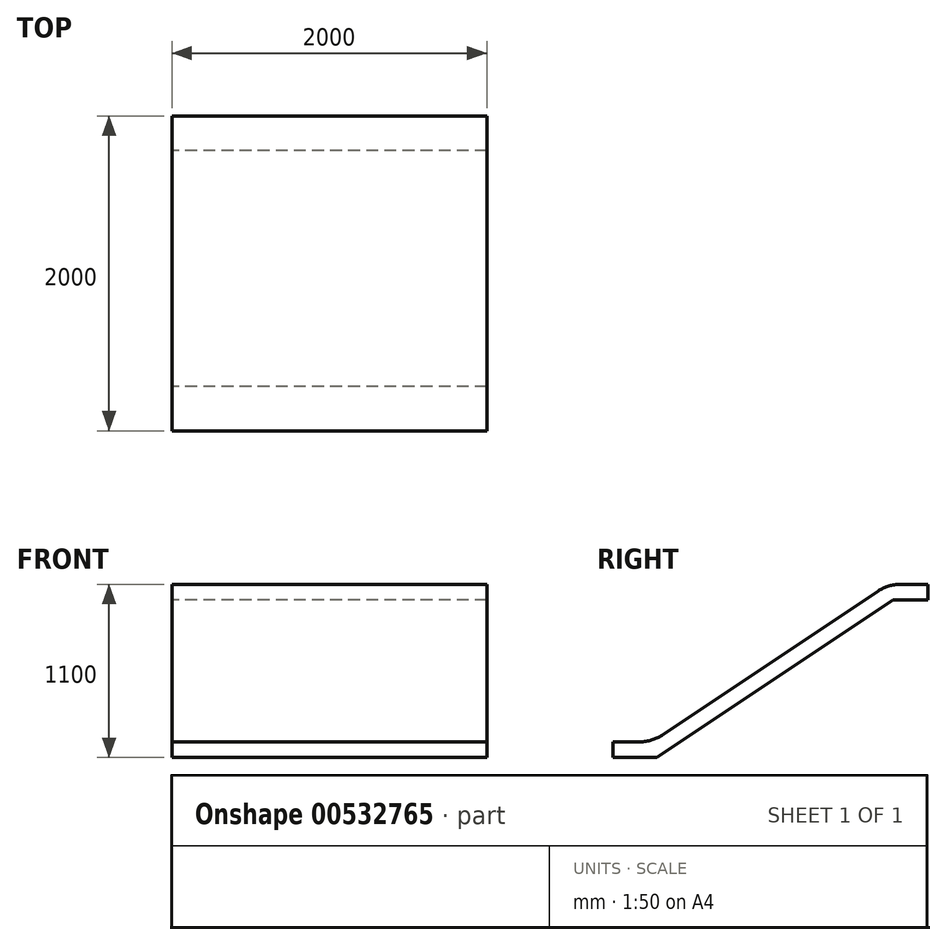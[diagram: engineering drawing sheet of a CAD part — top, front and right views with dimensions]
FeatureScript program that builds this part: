
annotation { "Feature Type Name" : "Feature", "Feature Type Description" : "" }
export const myFeature = defineFeature(function(context is Context, id is Id, definition is map)
    precondition{}
    {
        {
            var Q0;
            Q0=qCreatedBy(makeId("Right.planeOp"),FACE);
            var sketch = newSketch(context, id + "F0", { "sketchPlane" : qUnion([Q0])});
            skLineSegment(sketch, "E0", {"start": v(0, 0) * mm, "end": v(-250, 0) * mm});
            skLineSegment(sketch, "E1", {"start": v(-250, 0) * mm, "end": v(-1750, -1000) * mm});
            skLineSegment(sketch, "E2", {"start": v(-1750, -1000) * mm, "end": v(-2000, -1000) * mm});
            skLineSegment(sketch, "E3.0", {"start": v(-1719.72, -1100) * mm, "end": v(-2000, -1100) * mm});
            skLineSegment(sketch, "E3.1", {"start": v(-219.72, -100) * mm, "end": v(-1719.72, -1100) * mm});
            skLineSegment(sketch, "E3.2", {"start": v(0, -100) * mm, "end": v(-219.72, -100) * mm});
            skLineSegment(sketch, "E4", {"start": v(-2000, -1000) * mm, "end": v(-2000, -1100) * mm});
            skLineSegment(sketch, "E5", {"start": v(0, -100) * mm, "end": v(0, 0) * mm});
            skSolve(sketch);
        }
        {
            var Q0;
            Q0=makeQuery(id+"F0.imprint","IMPRINT",FACE,{"disambiguationData":[TD([[makeQuery(id+"F0.imprint","IMPRINT",EDGE,{"derivedFrom":sQuery(id+"F0.wireOp",EDGE,"E0")}),1.0]])]});
            extrude(context, id + "F1", {"entities" : qUnion([Q0]), "depth" : 2000 * mm, "offsetDistance" : 25 * mm});
        }
        {
            var Q0;
            Q0=makeQuery(id+"F1.opExtrude","SWEPT_EDGE",EDGE,{"disambiguationData":[OSD([sQuery(id+"F0.wireOp",EDGE,"E0"),sQuery(id+"F0.wireOp",EDGE,"E1")])]});
            var Q1;
            Q1=makeQuery(id+"F1.opExtrude","SWEPT_EDGE",EDGE,{"disambiguationData":[OSD([sQuery(id+"F0.wireOp",EDGE,"E1"),sQuery(id+"F0.wireOp",EDGE,"E2")])]});
            fillet(context, id + "F2", {"entities" : qUnion([Q0, Q1]), "radius" : 250 * mm, "tangentPropagation" : true, "allowEdgeOverflow" : false});
        }
    });
